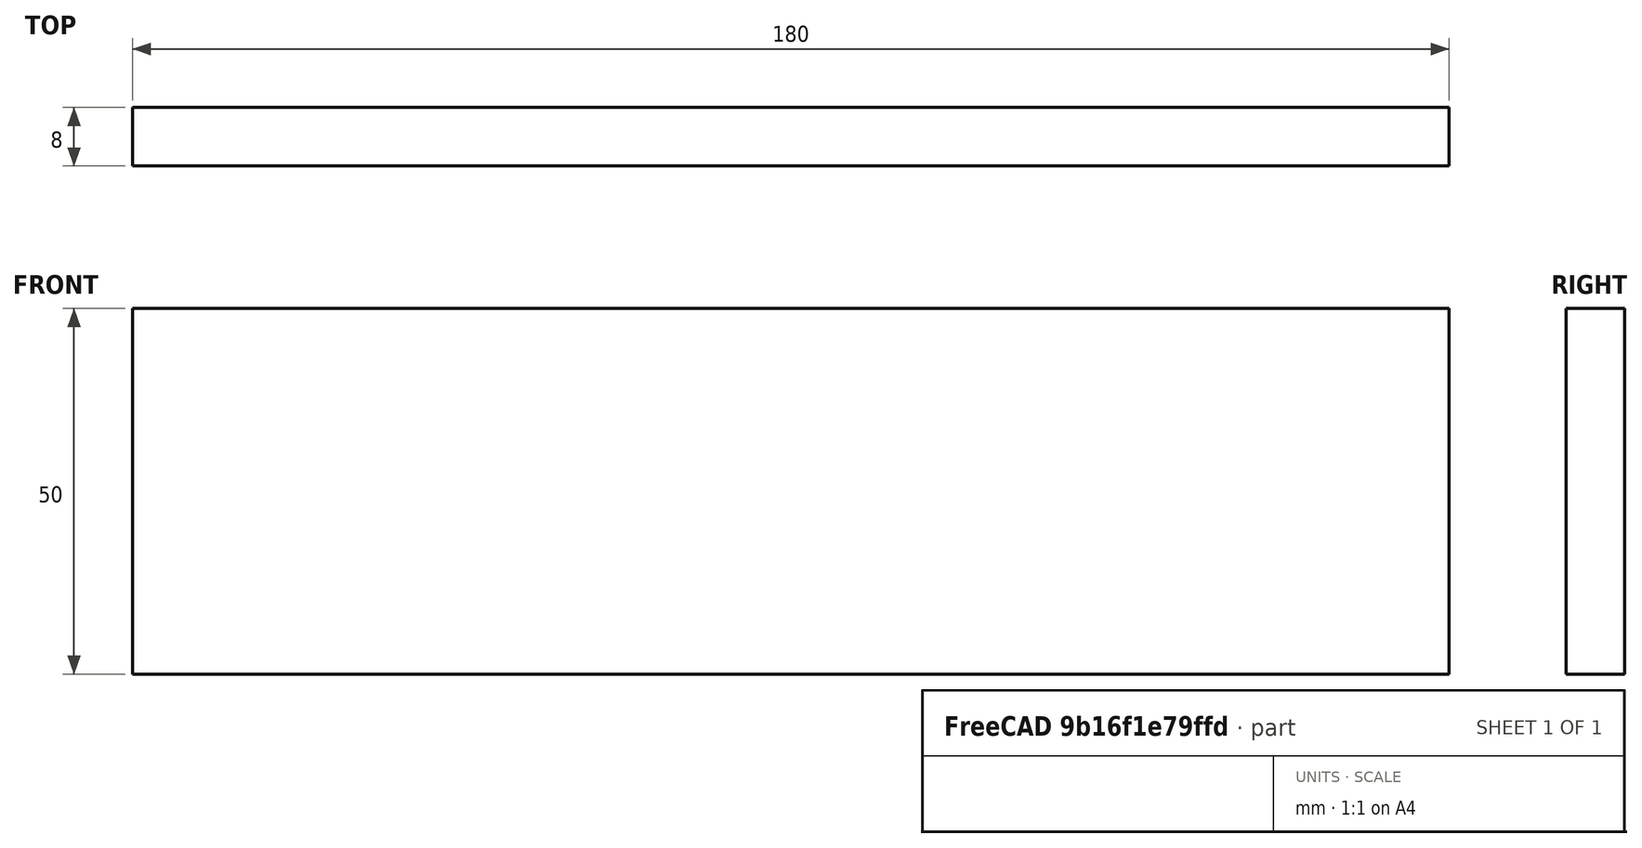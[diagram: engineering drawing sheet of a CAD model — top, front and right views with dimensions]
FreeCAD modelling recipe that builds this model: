
FCSTD DOCUMENT  (FreeCAD 0.15R4671 (Git))
Label: Flat Bar 180x8 EN10058 S235JR
License: All rights reserved
LicenseURL: http://en.wikipedia.org/wiki/All_rights_reserved
objects: Sketcher::SketchObject×1, Part::Extrusion×1
note: 2 computed .brp shape members not serialized (recipe doc carries the construction recipe); baked Part::Feature solids carry a one-line shape summary decoded from their .brp

FEATURE [Sketcher::SketchObject] Sketch
  sketch-geometry (4):
    g0: LineSegment StartX=-90 StartY=-4 StartZ=0 EndX=90 EndY=-4 EndZ=0
    g1: LineSegment StartX=90 StartY=-4 StartZ=0 EndX=90 EndY=4 EndZ=0
    g2: LineSegment StartX=90 StartY=4 StartZ=0 EndX=-90 EndY=4 EndZ=0
    g3: LineSegment StartX=-90 StartY=4 StartZ=0 EndX=-90 EndY=-4 EndZ=0
  constraints (12):
    c: Coincident(g0,g1)
    c: Coincident(g1,g2)
    c: Coincident(g2,g3)
    c: Coincident(g3,g0)
    c: Horizontal(g0)
    c: Horizontal(g2)
    c: Vertical(g1)
    c: Vertical(g3)
    c: Symmetric(g1,g2,g-2)
    c: Symmetric(g0,g1,g-1)
    c: DistanceY(g1) = 8
    c: DistanceX(g0) = 180
FEATURE [Part::Extrusion] Extrude  label="Flat Bar 180x8 EN10058 S235JR"
  Base = -> Sketch
  Dir = (0,0,50)
  Solid = true
